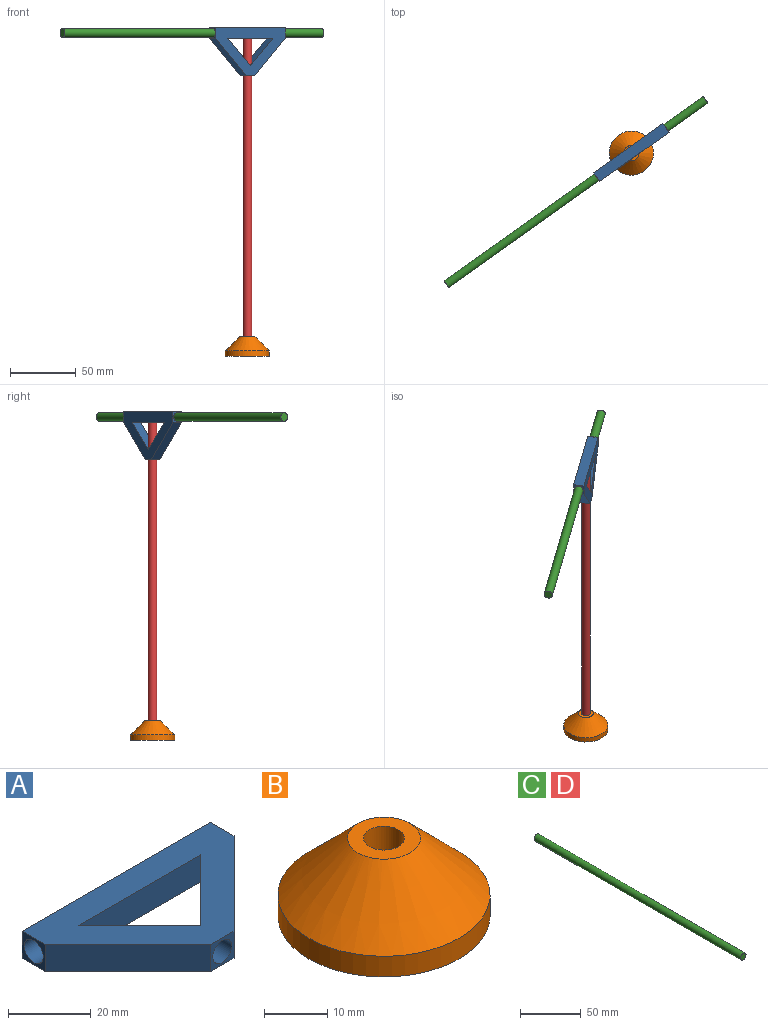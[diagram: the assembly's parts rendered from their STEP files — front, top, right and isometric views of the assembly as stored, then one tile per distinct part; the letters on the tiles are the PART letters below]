
ASSEMBLY  parts=4 mates=3
PART A: 13 faces, bbox 64.6x36.3x8 mm
  f0: plane 64.57x8mm, normal (0,1,0), area 516.5mm2, adj f1,f8,f9,f10
  f1: plane 8x8mm, normal (-1,0,0), area 30.8mm2, adj f0,f2,f9,f10,f12
  f2: plane 28.28x28.28mm, normal (-0.71,-0.71,0), area 320mm2, adj f1,f3,f9,f10
  f3: plane 8x8mm, normal (0,-1,0), area 30.8mm2, adj f2,f4,f9,f10,f11
  f4: plane 28.28x28.28mm, normal (0.71,-0.71,0), area 320mm2, adj f3,f8,f9,f10
  f5: plane 20.97x20.97mm, normal (0.71,0.71,0), area 213.8mm2, adj f6,f7,f9,f10,f11
  f6: plane 41.94x8mm, normal (0,-1,0), area 335.5mm2, adj f5,f7,f9,f10
  f7: plane 20.97x20.97mm, normal (-0.71,0.71,0), area 213.8mm2, adj f5,f6,f9,f10,f11
  f8: plane 8x8mm, normal (1,0,0), area 30.8mm2, adj f0,f4,f9,f10,f12
  f9: plane 64.57x36.28mm, normal (0,0,1), area 1103.1mm2, adj f0,f1,f2,f3,f4,f5,f6,f7
  f10: plane 64.57x36.28mm, normal (0,0,-1), area 1103.1mm2, adj f0,f1,f2,f3,f4,f5,f6,f7
  f11: cylinder r=3.25mm len=10.57mm, axis (0,-1,0), area 191.6mm2, adj f3,f5,f7
  f12: cylinder r=3.25mm len=64.57mm, axis (1,0,0), area 1318.5mm2, adj f1,f8
PART B: 5 faces, bbox 33.5x33.5x15 mm
  f0: cylinder r=3.25mm len=15mm, axis (0,0,-1), area 306.3mm2, adj f1,f4
  f1: plane 33.5x33.5mm, normal (0,0,-1), area 848.2mm2, adj f0,f2
  f2: cylinder r=16.75mm len=33.5mm, axis (0,0,-1), area 421mm2, adj f1,f3
  f3: cone r=16.75mm half-angle=45deg, axis (0,0,-1), area 1099.6mm2, adj f2,f4
  f4: plane 11.5x11.5mm, normal (0,0,1), area 70.7mm2, adj f0,f3
PART C: 3 faces, bbox 6.5x241.3x6.5 mm
  f0: cylinder r=3.25mm len=241.3mm, axis (0,1,0), area 4927.4mm2, adj f1,f2
  f1: plane 6.5x6.5mm, normal (0,-1,0), area 33.2mm2, adj f0
  f2: plane 6.5x6.5mm, normal (0,1,0), area 33.2mm2, adj f0
PART D: same geometry as C
PLACE A rot(axis=(0.22,-0.69,-0.69),155.1deg) t=(-41.21,32.65,139.98)mm
PLACE B t=(-43.53,35.91,-80.35)mm fixed
PLACE C rot(axis=(0,0,1),125.5deg) t=(-183.83,-64.02,164.95)mm
PLACE D rot(axis=(1,0,0),90deg) t=(-43.53,35.91,160.95)mm fixed
MATE slider C.f0 <-> A.f12  axis (-0.81,-0.58,0) through (-85.56,5.98,164.95)mm
MATE planar D.f0 <-> A.f11  axis (0,0,1) through (-43.53,35.91,160.95)mm
MATE cylindrical D.f0 <-> A.f11  axis (0,0,1) through (-43.53,35.91,40.3)mm
